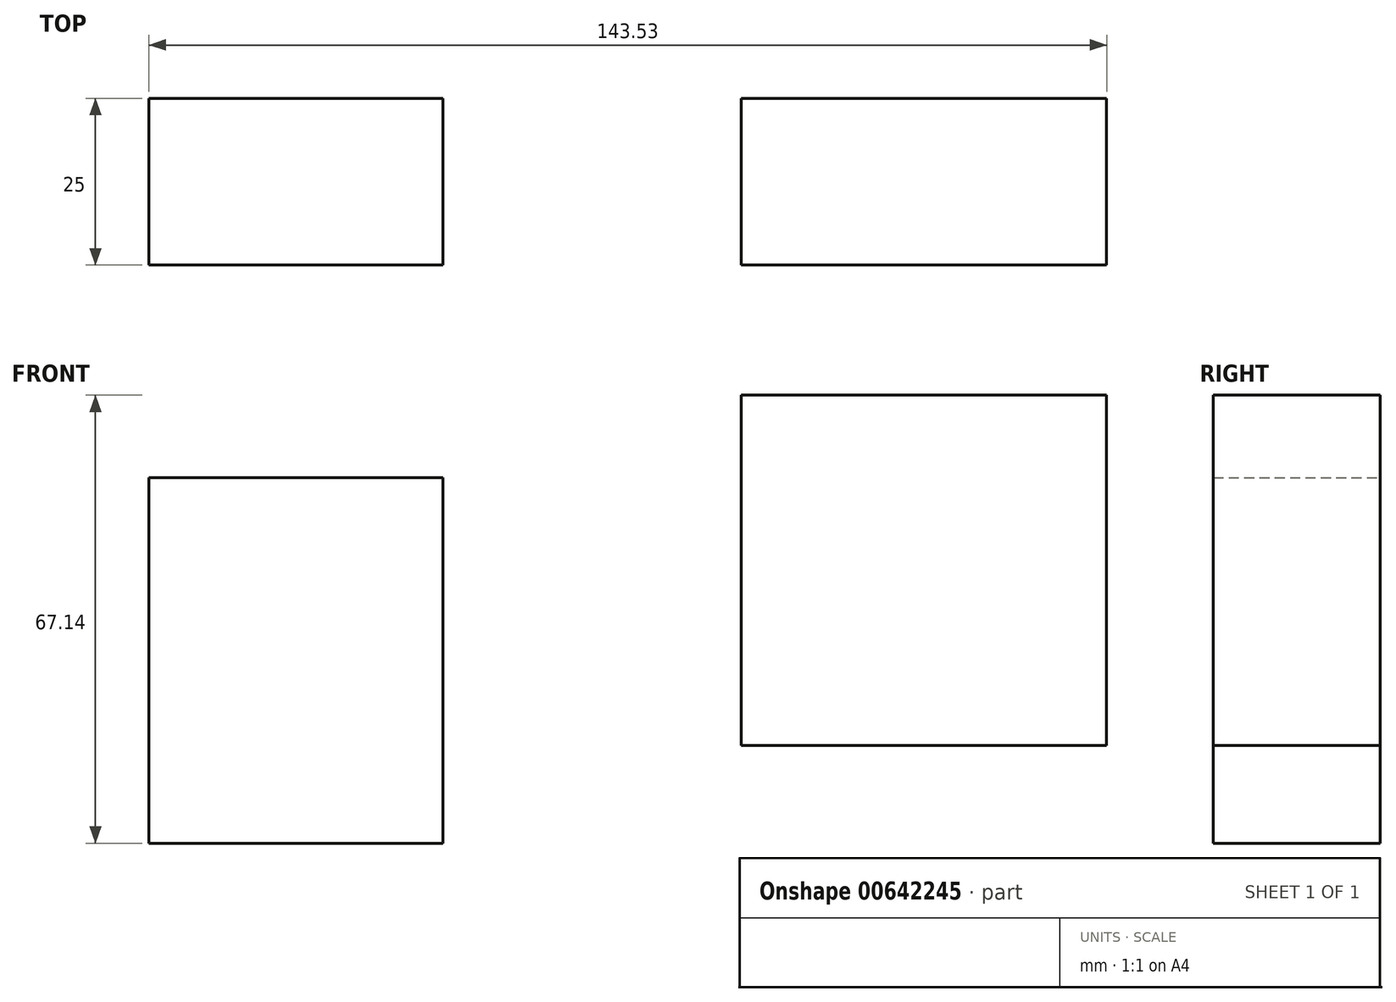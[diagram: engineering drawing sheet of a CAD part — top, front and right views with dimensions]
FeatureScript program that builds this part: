
annotation { "Feature Type Name" : "Feature", "Feature Type Description" : "" }
export const myFeature = defineFeature(function(context is Context, id is Id, definition is map)
    precondition{}
    {
        {
            var Q0;
            Q0=qCreatedBy(makeId("Front.planeOp"),FACE);
            var sketch = newSketch(context, id + "F0", { "sketchPlane" : qUnion([Q0])});
            skLineSegment(sketch, "E0.bottom", {"start": v(-102.97, 18.17) * mm, "end": v(-58.91, 18.17) * mm});
            skLineSegment(sketch, "E0.top", {"start": v(-102.97, 72.95) * mm, "end": v(-58.91, 72.95) * mm});
            skLineSegment(sketch, "E0.left", {"start": v(-102.97, 18.17) * mm, "end": v(-102.97, 72.95) * mm});
            skLineSegment(sketch, "E0.right", {"start": v(-58.91, 18.17) * mm, "end": v(-58.91, 72.95) * mm});
            skPoint(sketch, "E0.middle", {"position": v(-80.94, 45.56) * mm});
            skLineSegment(sketch, "E1.bottom", {"start": v(-14.19, 32.79) * mm, "end": v(40.56, 32.79) * mm});
            skLineSegment(sketch, "E1.top", {"start": v(-14.19, 85.3) * mm, "end": v(40.56, 85.3) * mm});
            skLineSegment(sketch, "E1.left", {"start": v(-14.19, 32.79) * mm, "end": v(-14.19, 85.3) * mm});
            skLineSegment(sketch, "E1.right", {"start": v(40.56, 32.79) * mm, "end": v(40.56, 85.3) * mm});
            skPoint(sketch, "E1.middle", {"position": v(13.18, 59.05) * mm});
            skSolve(sketch);
        }
        {
            var Q0;
            Q0=makeQuery(id+"F0.imprint","IMPRINT",FACE,{"disambiguationData":[TD([[makeQuery(id+"F0.imprint","IMPRINT",EDGE,{"derivedFrom":sQuery(id+"F0.wireOp",EDGE,"E0.bottom")}),1.0]])]});
            var Q1;
            Q1=makeQuery(id+"F0.imprint","IMPRINT",FACE,{"disambiguationData":[TD([[makeQuery(id+"F0.imprint","IMPRINT",EDGE,{"derivedFrom":sQuery(id+"F0.wireOp",EDGE,"E1.bottom")}),1.0]])]});
            extrude(context, id + "F1", {"entities" : qUnion([Q0, Q1]), "depth" : 25 * mm, "offsetDistance" : 25 * mm});
        }
    });
